FCSTD DOCUMENT  (FreeCAD 0.19R0.19.2)
Label: laptopStand016
License: All rights reserved
LicenseURL: http://en.wikipedia.org/wiki/All_rights_reserved
objects: Sketcher::SketchObject×1
note: 1 computed .brp shape members not serialized (recipe doc carries the construction recipe); baked Part::Feature solids carry a one-line shape summary decoded from their .brp

FEATURE [Sketcher::SketchObject] Sketch
  FullyConstrained = true
  sketch-geometry (52):
    g0: LineSegment StartX=-22.9272 StartY=136.221 StartZ=0 EndX=-22.9272 EndY=-103.779 EndZ=0
    g1: LineSegment StartX=-22.9272 StartY=136.221 StartZ=0 EndX=387.073 EndY=136.221 EndZ=0
    g2: LineSegment StartX=-22.9272 StartY=-103.779 StartZ=0 EndX=387.073 EndY=-103.779 EndZ=0
    g3: LineSegment StartX=387.073 StartY=136.221 StartZ=0 EndX=387.073 EndY=-103.779 EndZ=0
    g4: LineSegment StartX=375.073 StartY=115.221 StartZ=0 EndX=318.073 EndY=83.9235 EndZ=0
    g5: LineSegment StartX=-10.9272 StartY=-82.7794 StartZ=0 EndX=46.0728 EndY=-51.4823 EndZ=0
    g6: LineSegment StartX=-1.92719 StartY=124.221 StartZ=0 EndX=46.0728 EndY=97.8651 EndZ=0
    g7: LineSegment StartX=366.073 StartY=-91.7794 StartZ=0 EndX=318.073 EndY=-65.424 EndZ=0
    g8: LineSegment StartX=-10.9272 StartY=115.221 StartZ=0 EndX=-10.9272 EndY=-82.7794 EndZ=0
    g9: LineSegment StartX=375.073 StartY=-82.7794 StartZ=0 EndX=375.073 EndY=115.221 EndZ=0
    g10: LineSegment StartX=-1.92719 StartY=-91.7794 StartZ=0 EndX=46.0728 EndY=-91.7794 EndZ=0
    g11: LineSegment StartX=318.073 StartY=124.221 StartZ=0 EndX=366.073 EndY=124.221 EndZ=0
    g12: LineSegment StartX=306.073 StartY=-81.8102 StartZ=0 EndX=224.513 EndY=-14.0532 EndZ=0
    g13: LineSegment StartX=58.0728 StartY=114.251 StartZ=0 EndX=139.632 EndY=46.4944 EndZ=0
    g14: LineSegment StartX=306.073 StartY=124.221 StartZ=0 EndX=189.124 EndY=27.0628 EndZ=0
    g15: LineSegment StartX=58.0728 StartY=-91.7794 StartZ=0 EndX=175.022 EndY=5.37834 EndZ=0
    g16: LineSegment StartX=46.0728 StartY=124.221 StartZ=0 EndX=46.0728 EndY=97.8651 EndZ=0
    g17: LineSegment StartX=58.0728 StartY=-81.8102 StartZ=0 EndX=58.0728 EndY=-58.8351 EndZ=0
    g18: LineSegment StartX=318.073 StartY=124.221 StartZ=0 EndX=318.073 EndY=97.8651 EndZ=0
    g19: LineSegment StartX=306.073 StartY=114.251 StartZ=0 EndX=306.073 EndY=91.2763 EndZ=0
    g20: LineSegment StartX=182.073 StartY=23.1914 StartZ=0 EndX=189.124 EndY=27.0628 EndZ=0
    g21: LineSegment StartX=182.073 StartY=9.24976 StartZ=0 EndX=175.022 EndY=5.37834 EndZ=0
    g22: LineSegment StartX=224.513 StartY=46.4944 StartZ=0 EndX=306.073 EndY=114.251 EndZ=0
    g23: LineSegment StartX=175.022 StartY=27.0628 StartZ=0 EndX=58.0728 EndY=124.221 EndZ=0
    g24: LineSegment StartX=169.377 StartY=16.2206 StartZ=0 EndX=58.0728 EndY=77.3346 EndZ=0
    g25: LineSegment StartX=139.632 StartY=-14.0532 StartZ=0 EndX=58.0728 EndY=-81.8102 EndZ=0
    g26: LineSegment StartX=194.768 StartY=16.2206 StartZ=0 EndX=306.073 EndY=-44.8935 EndZ=0
    g27: LineSegment StartX=224.513 StartY=46.4944 StartZ=0 EndX=306.073 EndY=91.2763 EndZ=0
    g28: LineSegment StartX=175.022 StartY=27.0628 StartZ=0 EndX=182.073 EndY=23.1914 EndZ=0
    g29: LineSegment StartX=139.632 StartY=-14.0532 StartZ=0 EndX=58.0728 EndY=-58.8351 EndZ=0
    g30: LineSegment StartX=189.124 StartY=5.37834 StartZ=0 EndX=182.073 EndY=9.24976 EndZ=0
    g31: LineSegment StartX=189.124 StartY=5.37834 StartZ=0 EndX=306.073 EndY=-91.7794 EndZ=0
    g32: LineSegment StartX=306.073 StartY=77.3346 StartZ=0 EndX=306.073 EndY=-44.8935 EndZ=0
    g33: LineSegment StartX=318.073 StartY=83.9235 StartZ=0 EndX=318.073 EndY=-51.4823 EndZ=0
    g34: LineSegment StartX=318.073 StartY=97.8651 StartZ=0 EndX=366.073 EndY=124.221 EndZ=0
    g35: LineSegment StartX=306.073 StartY=77.3346 StartZ=0 EndX=194.768 EndY=16.2206 EndZ=0
    g36: LineSegment StartX=306.073 StartY=-58.8351 StartZ=0 EndX=224.513 EndY=-14.0532 EndZ=0
    g37: LineSegment StartX=306.073 StartY=-58.8351 StartZ=0 EndX=306.073 EndY=-81.8102 EndZ=0
    g38: LineSegment StartX=318.073 StartY=-51.4823 StartZ=0 EndX=375.073 EndY=-82.7794 EndZ=0
    g39: LineSegment StartX=318.073 StartY=-65.424 StartZ=0 EndX=318.073 EndY=-91.7794 EndZ=0
    g40: LineSegment StartX=306.073 StartY=124.221 StartZ=0 EndX=58.0728 EndY=124.221 EndZ=0
    g41: LineSegment StartX=318.073 StartY=-91.7794 StartZ=0 EndX=366.073 EndY=-91.7794 EndZ=0
    g42: LineSegment StartX=58.0728 StartY=-91.7794 StartZ=0 EndX=306.073 EndY=-91.7794 EndZ=0
    g43: LineSegment StartX=58.0728 StartY=-44.8935 StartZ=0 EndX=58.0728 EndY=77.3346 EndZ=0
    g44: LineSegment StartX=46.0728 StartY=-65.424 StartZ=0 EndX=-1.92719 EndY=-91.7794 EndZ=0
    g45: LineSegment StartX=46.0728 StartY=-65.424 StartZ=0 EndX=46.0728 EndY=-91.7794 EndZ=0
    g46: LineSegment StartX=58.0728 StartY=-44.8935 StartZ=0 EndX=169.377 EndY=16.2206 EndZ=0
    g47: LineSegment StartX=58.0728 StartY=91.2763 StartZ=0 EndX=58.0728 EndY=114.251 EndZ=0
    g48: LineSegment StartX=46.0728 StartY=83.9235 StartZ=0 EndX=46.0728 EndY=-51.4823 EndZ=0
    g49: LineSegment StartX=46.0728 StartY=124.221 StartZ=0 EndX=-1.92719 EndY=124.221 EndZ=0
    g50: LineSegment StartX=58.0728 StartY=91.2763 StartZ=0 EndX=139.632 EndY=46.4944 EndZ=0
    g51: LineSegment StartX=46.0728 StartY=83.9235 StartZ=0 EndX=-10.9272 EndY=115.221 EndZ=0
  constraints (102):
    c: Vertical(g0)
    c: Distance(g0) = 240
    c: Horizontal(g1)
    c: Distance(g1) = 410
    c: Coincident(g1,g0)
    c: Coincident(g2,g0)
    c: Horizontal(g2)
    c: Coincident(g3,g1)
    c: Vertical(g3)
    c: Coincident(g2,g3)
    c: Block(g1)
    c: Horizontal(g10)
    c: Horizontal(g11)
    c: PointOnObject(g35,g6)
    c: Coincident(g28,g20)
    c: Coincident(g30,g21)
    c: Tangent(g7,g24)
    c: PointOnObject(g24,g5)
    c: PointOnObject(g26,g4)
    c: Coincident(g20,g14)
    c: Tangent(g20,g27)
    c: Coincident(g50,g13)
    c: Coincident(g28,g23)
    c: Coincident(g22,g27)
    c: Coincident(g21,g15)
    c: Coincident(g29,g25)
    c: Tangent(g21,g29)
    c: Coincident(g36,g12)
    c: Coincident(g31,g30)
    c: Coincident(g22,g19)
    c: Tangent(g19,g32)
    c: Tangent(g18,g33)
    c: Coincident(g27,g19)
    c: Tangent(g27,g34)
    c: Coincident(g4,g33)
    c: Coincident(g35,g32)
    c: Tangent(g4,g35)
    c: Coincident(g37,g12)
    c: Tangent(g7,g36)
    c: Tangent(g32,g37)
    c: Coincident(g26,g32)
    c: Tangent(g26,g38)
    c: Coincident(g33,g38)
    c: Coincident(g39,g7)
    c: Tangent(g33,g39)
    c: Coincident(g25,g17)
    c: Tangent(g17,g43)
    c: Coincident(g29,g17)
    c: Tangent(g29,g44)
    c: Coincident(g45,g44)
    c: Tangent(g16,g45)
    c: Coincident(g5,g48)
    c: Coincident(g46,g43)
    c: Tangent(g5,g46)
    c: Tangent(g43,g47)
    c: Tangent(g16,g48)
    c: Coincident(g13,g47)
    c: PointOnObject(g40,g23)
    c: Tangent(g40,g49)
    c: Coincident(g6,g16)
    c: Coincident(g50,g47)
    c: Tangent(g6,g50)
    c: Coincident(g24,g43)
    c: Coincident(g51,g48)
    c: Tangent(g24,g51)
    c: Block(g23)
    c: Block(g14)
    c: Block(g20)
    c: Block(g40)
    c: Block(g18)
    c: Block(g34)
    c: Block(g4)
    c: Block(g38)
    c: Block(g9)
    c: Block(g36)
    c: Block(g37)
    c: Block(g7)
    c: Block(g39)
    c: Block(g22)
    c: Block(g31)
    c: Block(g42)
    c: Block(g21)
    c: Block(g15)
    c: Block(g29)
    c: Block(g25)
    c: Block(g45)
    c: Block(g44)
    c: Block(g5)
    c: Block(g8)
    c: Block(g51)
    c: Block(g6)
    c: Block(g16)
    c: Block(g13)
    c: Block(g47)
    c: Block(g35)
    c: Block(g32)
    c: Block(g24)
    c: Block(g46)
    c: Block(g49)
    c: Block(g11)
    c: Block(g41)
    c: Block(g10)
